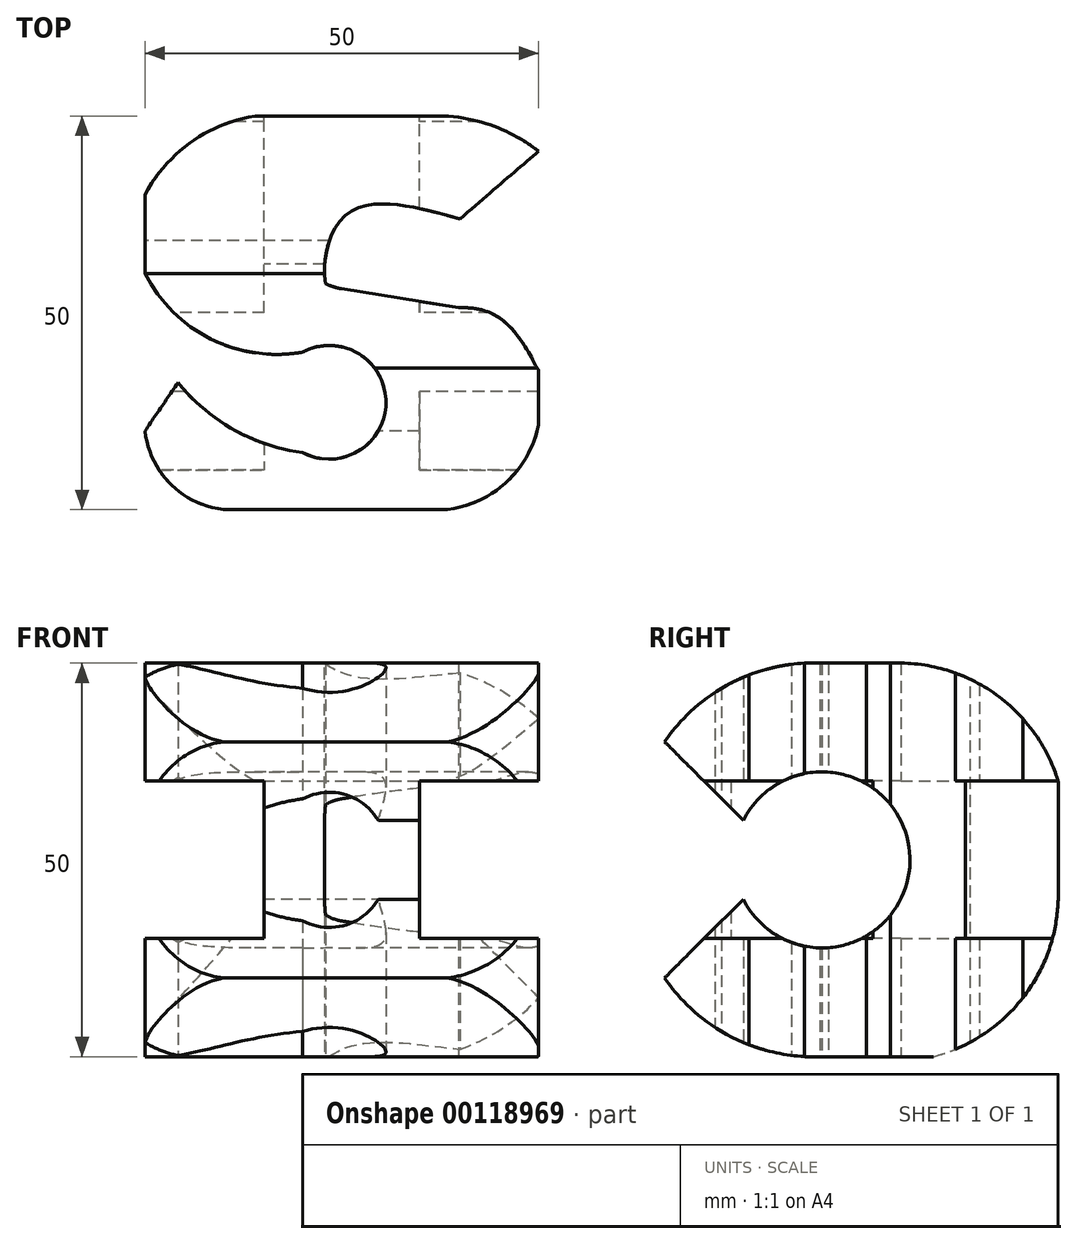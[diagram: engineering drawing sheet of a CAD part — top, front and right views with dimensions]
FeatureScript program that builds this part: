
annotation { "Feature Type Name" : "Feature", "Feature Type Description" : "" }
export const myFeature = defineFeature(function(context is Context, id is Id, definition is map)
    precondition{}
    {
        {
            var Q0;
            Q0=qCreatedBy(makeId("Front.planeOp"),FACE);
            var sketch = newSketch(context, id + "F0", { "sketchPlane" : qUnion([Q0])});
            skLineSegment(sketch, "E0.bottom", {"start": v(25, 25) * mm, "end": v(-25, 25) * mm, "construction": true});
            skLineSegment(sketch, "E0.top", {"start": v(25, -25) * mm, "end": v(-25, -25) * mm, "construction": true});
            skLineSegment(sketch, "E0.left", {"start": v(25, 25) * mm, "end": v(25, -25) * mm, "construction": true});
            skLineSegment(sketch, "E0.right", {"start": v(-25, 25) * mm, "end": v(-25, -25) * mm, "construction": true});
            skPoint(sketch, "E0.middle", {"position": v(0, 0) * mm});
            skLineSegment(sketch, "E1", {"start": v(-15, 25) * mm, "end": v(-15, -25) * mm, "construction": true});
            skLineSegment(sketch, "E2", {"start": v(-5, 25) * mm, "end": v(-5, -25) * mm, "construction": true});
            skLineSegment(sketch, "E3", {"start": v(15, 22.54) * mm, "end": v(15, -25) * mm, "construction": true});
            skLineSegment(sketch, "E4", {"start": v(5, 25) * mm, "end": v(5, -27.33) * mm, "construction": true});
            skLineSegment(sketch, "E5", {"start": v(-25, 15) * mm, "end": v(25, 15) * mm, "construction": true});
            skLineSegment(sketch, "E6", {"start": v(-25, 5) * mm, "end": v(25, 5) * mm, "construction": true});
            skLineSegment(sketch, "E7", {"start": v(-25, -5) * mm, "end": v(25, -5) * mm, "construction": true});
            skLineSegment(sketch, "E8", {"start": v(-25, -15) * mm, "end": v(25, -15) * mm, "construction": true});
            skLineSegment(sketch, "E9", {"start": v(-25, -10) * mm, "end": v(-9.86, -10) * mm});
            skLineSegment(sketch, "E10", {"start": v(-25, 10) * mm, "end": v(-9.86, 10) * mm});
            skLineSegment(sketch, "E11", {"start": v(25, 10) * mm, "end": v(9.86, 10) * mm});
            skLineSegment(sketch, "E12", {"start": v(25, -10) * mm, "end": v(9.86, -10) * mm});
            skLineSegment(sketch, "E13", {"start": v(9.86, 10) * mm, "end": v(9.86, -10) * mm});
            skLineSegment(sketch, "E14", {"start": v(-9.86, 10) * mm, "end": v(-9.86, -10) * mm});
            skLineSegment(sketch, "E15", {"start": v(-25, 10) * mm, "end": v(-25, 25) * mm});
            skLineSegment(sketch, "E16", {"start": v(-25, 25) * mm, "end": v(25, 25) * mm});
            skLineSegment(sketch, "E17", {"start": v(25, 10) * mm, "end": v(25, 25) * mm});
            skLineSegment(sketch, "E18", {"start": v(-25, -25) * mm, "end": v(25, -25) * mm});
            skLineSegment(sketch, "E19", {"start": v(-25, -10) * mm, "end": v(-25, -25) * mm});
            skLineSegment(sketch, "E20", {"start": v(25, -10) * mm, "end": v(25, -25) * mm});
            skSolve(sketch);
        }
        {
            var Q0;
            Q0=qCreatedBy(makeId("Right.planeOp"),FACE);
            var sketch = newSketch(context, id + "F1", { "sketchPlane" : qUnion([Q0])});
            skLineSegment(sketch, "E21.bottom", {"start": v(-25, 25) * mm, "end": v(25, 25) * mm, "construction": true});
            skLineSegment(sketch, "E21.top", {"start": v(-25, -25) * mm, "end": v(25, -25) * mm, "construction": true});
            skLineSegment(sketch, "E21.left", {"start": v(-25, 25) * mm, "end": v(-25, -25) * mm, "construction": true});
            skLineSegment(sketch, "E21.right", {"start": v(25, 25) * mm, "end": v(25, -25) * mm, "construction": true});
            skPoint(sketch, "E21.middle", {"position": v(0, 0) * mm});
            skLineSegment(sketch, "E22", {"start": v(15, 25) * mm, "end": v(15, -25) * mm, "construction": true});
            skLineSegment(sketch, "E23", {"start": v(5, 25) * mm, "end": v(5, -25) * mm, "construction": true});
            skLineSegment(sketch, "E24", {"start": v(-5, 25) * mm, "end": v(-5, -25) * mm, "construction": true});
            skLineSegment(sketch, "E25", {"start": v(-15, 25) * mm, "end": v(-15, -25) * mm, "construction": true});
            skLineSegment(sketch, "E26", {"start": v(25, 15) * mm, "end": v(-25, 15) * mm, "construction": true});
            skLineSegment(sketch, "E27", {"start": v(25, 5) * mm, "end": v(-25, 5) * mm, "construction": true});
            skPoint(sketch, "E27.endSnap0", {"position": v(-25, 0) * mm});
            skLineSegment(sketch, "E28", {"start": v(25, -5) * mm, "end": v(-25, -5) * mm, "construction": true});
            skLineSegment(sketch, "E29", {"start": v(25, -15) * mm, "end": v(-25, -15) * mm, "construction": true});
            skArc(sketch, "E30", {"start": v(-25, -15) * mm, "mid": v(-16.3, -22.6) * mm, "end": v(-5, -25) * mm});
            skArc(sketch, "E31", {"start": v(-5, 25) * mm, "mid": v(-16.3, 22.6) * mm, "end": v(-25, 15) * mm});
            skLineSegment(sketch, "E32", {"start": v(-25, 15) * mm, "end": v(-15, 5) * mm});
            skLineSegment(sketch, "E33", {"start": v(-25, -15) * mm, "end": v(-15, -5) * mm});
            skArc(sketch, "E34", {"start": v(-15, -5) * mm, "mid": v(6.18, 0) * mm, "end": v(-15, 5) * mm});
            skArc(sketch, "E35", {"start": v(25, 9.98) * mm, "mid": v(17.45, 20.75) * mm, "end": v(5, 25) * mm});
            skArc(sketch, "E36", {"start": v(9.15, -25) * mm, "mid": v(20.42, -17.65) * mm, "end": v(25, -5) * mm});
            skLineSegment(sketch, "E37", {"start": v(5, 25) * mm, "end": v(-5, 25) * mm});
            skLineSegment(sketch, "E38", {"start": v(25, 9.98) * mm, "end": v(25, -5) * mm});
            skLineSegment(sketch, "E39", {"start": v(9.15, -25) * mm, "end": v(-5, -25) * mm});
            skSolve(sketch);
        }
        {
            var Q0;
            Q0=qCreatedBy(makeId("Top.planeOp"),FACE);
            var sketch = newSketch(context, id + "F2", { "sketchPlane" : qUnion([Q0])});
            skPoint(sketch, "E40.middle", {"position": v(0, 0) * mm});
            skLineSegment(sketch, "E41", {"start": v(15, -25) * mm, "end": v(14.72, -23.57) * mm, "construction": true});
            skLineSegment(sketch, "E42", {"start": v(-25, 15) * mm, "end": v(25, 15) * mm, "construction": true});
            skLineSegment(sketch, "E43", {"start": v(-25, 5) * mm, "end": v(25, 5) * mm, "construction": true});
            skLineSegment(sketch, "E44", {"start": v(-25, -5) * mm, "end": v(25, -5) * mm, "construction": true});
            skLineSegment(sketch, "E45", {"start": v(-25, -15) * mm, "end": v(25, -15) * mm, "construction": true});
            skLineSegment(sketch, "E46", {"start": v(25, -15) * mm, "end": v(24.12, -13.9) * mm, "construction": true});
            skArc(sketch, "E47", {"start": v(25, 20.52) * mm, "mid": v(18.58, 23.97) * mm, "end": v(11.37, 25) * mm});
            skArc(sketch, "E48", {"start": v(-5, 25) * mm, "mid": v(-16.6, 23.2) * mm, "end": v(-25, 15) * mm});
            skArc(sketch, "E49", {"start": v(-25, 5) * mm, "mid": v(-16.66, -3.31) * mm, "end": v(-5, -5) * mm});
            skLineSegment(sketch, "E50", {"start": v(25, 20.52) * mm, "end": v(15, 11.92) * mm});
            skPoint(sketch, "E51.1.internal.snap0", {"position": v(0, 15) * mm});
            skFitSpline(sketch, "E52.trimOffspring", {"points": [v(15, 11.92) * mm, v(0, 11.92) * mm, v(0, 0) * mm, v(18.86, 0) * mm, v(25, -7.2) * mm, v(25, -5) * mm], "startDerivative": vector(-75.12, 20.8) * mm, "endDerivative": vector(-3.54, 37.42) * mm});
            skArc(sketch, "E53", {"start": v(9.98, -25) * mm, "mid": v(24.5, -16.08) * mm, "end": v(18.86, 0) * mm});
            skArc(sketch, "E54", {"start": v(-5, -17.75) * mm, "mid": v(5.62, -11.37) * mm, "end": v(-5, -5) * mm});
            skArc(sketch, "E55", {"start": v(-20.8, -8.87) * mm, "mid": v(-13.75, -14.83) * mm, "end": v(-5, -17.75) * mm});
            skArc(sketch, "E56", {"start": v(-25, -15) * mm, "mid": v(-21.75, -21.75) * mm, "end": v(-15, -25) * mm});
            skLineSegment(sketch, "E57", {"start": v(-25, -15) * mm, "end": v(-20.8, -8.87) * mm});
            skLineSegment(sketch, "E58", {"start": v(18.86, 0) * mm, "end": v(0, 3.05) * mm});
            skPoint(sketch, "E58.endSnap0", {"position": v(0, 5) * mm});
            skArc(sketch, "E59", {"start": v(-5, 15) * mm, "mid": v(-5.82, 7.64) * mm, "end": v(0, 3.05) * mm});
            skArc(sketch, "E60", {"start": v(15, 11.92) * mm, "mid": v(5.48, 16.58) * mm, "end": v(-5, 15) * mm});
            skLineSegment(sketch, "E61", {"start": v(-5, 25) * mm, "end": v(11.37, 25) * mm});
            skLineSegment(sketch, "E62", {"start": v(-25, 15) * mm, "end": v(-25, 5) * mm});
            skLineSegment(sketch, "E63", {"start": v(-15, -25) * mm, "end": v(9.98, -25) * mm});
            skLineSegment(sketch, "E64", {"start": v(-5, 25) * mm, "end": v(15, 25) * mm});
            skLineSegment(sketch, "E65", {"start": v(-15, -25) * mm, "end": v(15, -25) * mm});
            skLineSegment(sketch, "E66", {"start": v(25, -7.2) * mm, "end": v(25, -15) * mm});
            skSolve(sketch);
        }
        {
            var Q0;
            Q0 = qSketchRegion(id + "F0", true);
            extrude(context, id + "F3", {"entities" : qUnion([Q0]), "endBound" : BoundingType.SYMMETRIC, "depth" : 50 * mm});
        }
        {
            var Q0;
            Q0 = qSketchRegion(id + "F1", true);
            extrude(context, id + "F4", {"entities" : qUnion([Q0]), "operationType" : NewBodyOperationType.INTERSECT, "endBound" : BoundingType.SYMMETRIC, "depth" : 50 * mm});
        }
        {
            var Q0;
            Q0 = qSketchRegion(id + "F2", true);
            extrude(context, id + "F5", {"entities" : qUnion([Q0]), "operationType" : NewBodyOperationType.INTERSECT, "endBound" : BoundingType.SYMMETRIC, "depth" : 50 * mm});
        }
    });
